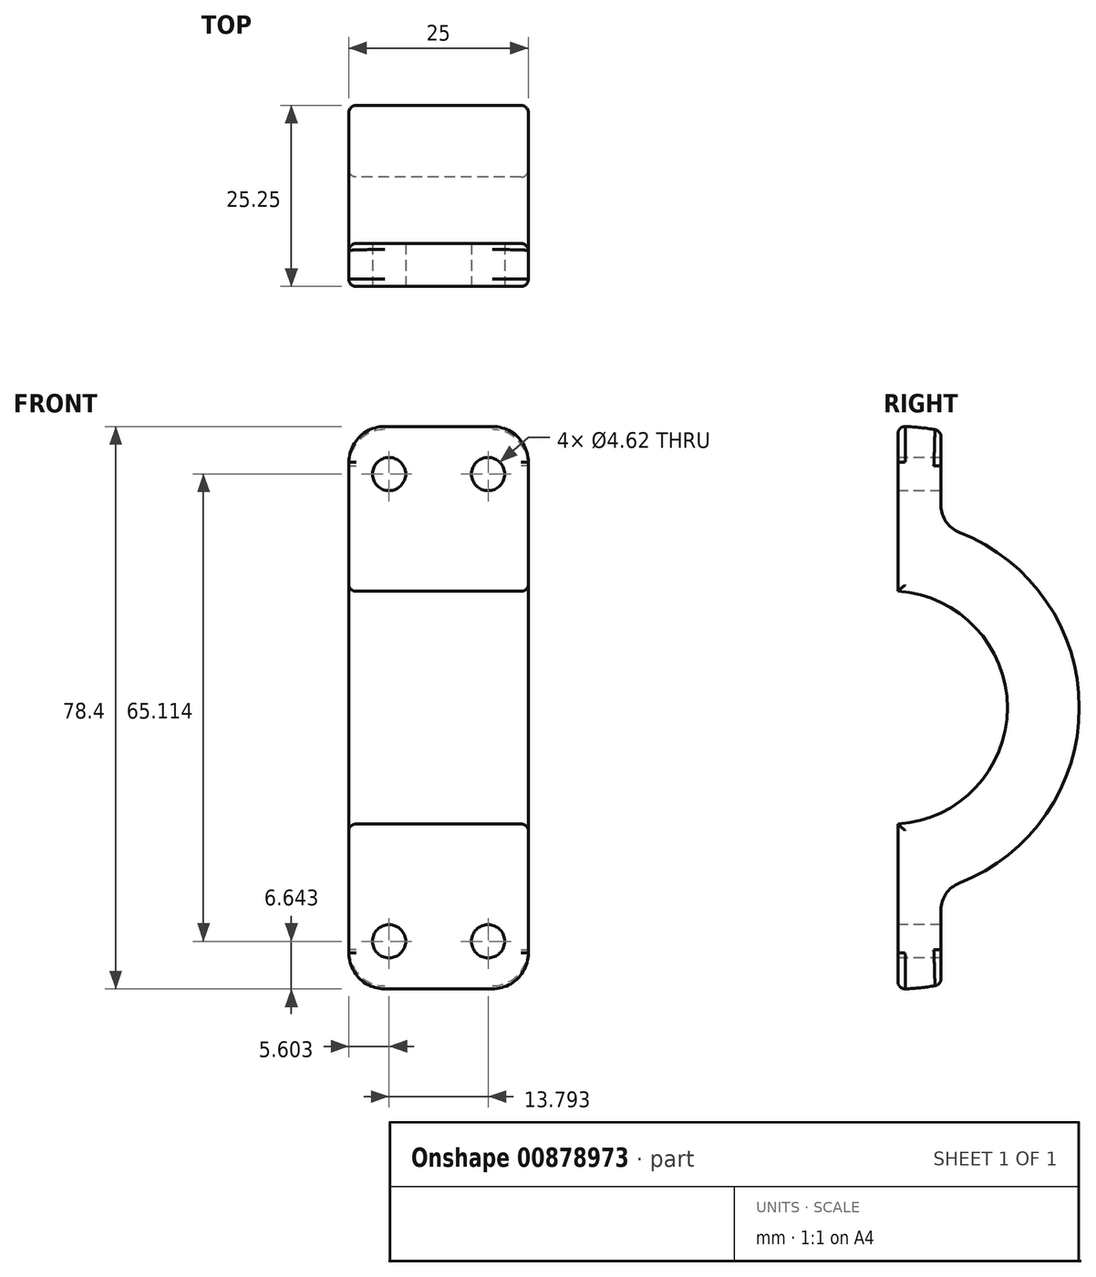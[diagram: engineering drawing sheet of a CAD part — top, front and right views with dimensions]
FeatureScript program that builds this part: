
annotation { "Feature Type Name" : "Feature", "Feature Type Description" : "" }
export const myFeature = defineFeature(function(context is Context, id is Id, definition is map)
    precondition{}
    {
        {
            var Q0;
            Q0=qCreatedBy(makeId("Right.planeOp"),FACE);
            var sketch = newSketch(context, id + "F0", { "sketchPlane" : qUnion([Q0])});
            skArc(sketch, "E0", {"start": v(1, -16.22) * mm, "mid": v(16.25, 0) * mm, "end": v(1, 16.22) * mm});
            skArc(sketch, "E1.0", {"start": v(9.54, -24.45) * mm, "mid": v(26.25, 0) * mm, "end": v(9.54, 24.45) * mm});
            skLineSegment(sketch, "E2.0", {"start": v(7, -28.18) * mm, "end": v(7, -38.62) * mm});
            skLineSegment(sketch, "E3.0", {"start": v(7, 28.18) * mm, "end": v(7, 38.62) * mm});
            skArc(sketch, "E4.0", {"start": v(1, -39.24) * mm, "mid": v(4.01, -39.04) * mm, "end": v(7, -38.62) * mm});
            skArc(sketch, "E5.trimOffspring", {"start": v(7, 38.62) * mm, "mid": v(4.01, 39.04) * mm, "end": v(1, 39.24) * mm});
            skPoint(sketch, "E6.visualSharp", {"position": v(-5, 25.77) * mm});
            skPoint(sketch, "E7.visualSharp", {"position": v(7, 25.3) * mm});
            skArc(sketch, "E7.filletArc", {"start": v(7, 28.18) * mm, "mid": v(7.7, 25.92) * mm, "end": v(9.54, 24.45) * mm});
            skPoint(sketch, "E8.visualSharp", {"position": v(7, -25.3) * mm});
            skArc(sketch, "E8.filletArc", {"start": v(9.54, -24.45) * mm, "mid": v(7.7, -25.92) * mm, "end": v(7, -28.18) * mm});
            skPoint(sketch, "E9.visualSharp", {"position": v(-5, -25.77) * mm});
            skLineSegment(sketch, "E10.0", {"start": v(1, 16.22) * mm, "end": v(1, 39.25) * mm});
            skLineSegment(sketch, "E11.0", {"start": v(1, -16.22) * mm, "end": v(1, -39.25) * mm});
            skSolve(sketch);
        }
        {
            var Q0;
            Q0=qSketchRegion(id+"F0",true);
            extrude(context, id + "F1", {"entities" : qUnion([Q0]), "endBound" : BoundingType.SYMMETRIC, "depth" : 25 * mm, "offsetDistance" : 25 * mm});
        }
        {
            var Q0;
            Q0=qCreatedBy(makeId("Front.planeOp"),FACE);
            var sketch = newSketch(context, id + "F2", { "sketchPlane" : qUnion([Q0])});
            skCircle(sketch, "E12", {"center": v(6.9, 32.56) * mm, "radius": 2.31 * mm});
            skCircle(sketch, "E13.MirrorC", {"center": v(-6.9, 32.56) * mm, "radius": 2.31 * mm});
            skCircle(sketch, "E14.MirrorC", {"center": v(-6.9, -32.56) * mm, "radius": 2.31 * mm});
            skCircle(sketch, "E15.MirrorC", {"center": v(6.9, -32.56) * mm, "radius": 2.31 * mm});
            skSolve(sketch);
        }
        {
            var Q0;
            Q0=qSketchRegion(id+"F2",true);
            extrude(context, id + "F3", {"entities" : qUnion([Q0]), "operationType" : NewBodyOperationType.REMOVE, "endBound" : BoundingType.THROUGH_ALL, "oppositeDirection" : true, "depth" : 25 * mm, "offsetDistance" : 25 * mm});
        }
        {
            var Q0;
            Q0=makeQuery(id+"F1.opExtrude","CAP_EDGE",EDGE,{"disambiguationData":[OSD([sQuery(id+"F0.wireOp",EDGE,"E5.trimOffspring")])],"isStart":false});
            var Q1;
            Q1=makeQuery(id+"F1.opExtrude","CAP_EDGE",EDGE,{"disambiguationData":[OSD([sQuery(id+"F0.wireOp",EDGE,"E5.trimOffspring")])],"isStart":true});
            var Q2;
            Q2=makeQuery(id+"F1.opExtrude","CAP_EDGE",EDGE,{"disambiguationData":[OSD([sQuery(id+"F0.wireOp",EDGE,"E4.0")])],"isStart":false});
            var Q3;
            Q3=makeQuery(id+"F1.opExtrude","CAP_EDGE",EDGE,{"disambiguationData":[OSD([sQuery(id+"F0.wireOp",EDGE,"E4.0")])],"isStart":true});
            fillet(context, id + "F4", {"entities" : qUnion([Q0, Q1, Q2, Q3]), "radius" : 5 * mm, "tangentPropagation" : true, "allowEdgeOverflow" : false});
        }
        {
            var Q0;
            Q0=makeQuery(id+"F1.opExtrude","CAP_FACE",FACE,{"disambiguationData":[OSD([sQuery(id+"F0.wireOp",EDGE,"E0"),sQuery(id+"F0.wireOp",EDGE,"E1.0"),sQuery(id+"F0.wireOp",EDGE,"g6IvzIde-RPpm-J4Ch-rFcU-dSb5MLyEbczB"),sQuery(id+"F0.wireOp",EDGE,"LpNSRWhE-LSOE-Vq07-Rzua-Ym4zSv88PilT"),sQuery(id+"F0.wireOp",EDGE,"E2.0"),sQuery(id+"F0.wireOp",EDGE,"E3.0"),sQuery(id+"F0.wireOp",EDGE,"E4.0"),sQuery(id+"F0.wireOp",EDGE,"E5.trimOffspring"),sQuery(id+"F0.wireOp",EDGE,"E7.filletArc"),sQuery(id+"F0.wireOp",EDGE,"E8.filletArc")])],"isStart":true});
            var Q1;
            Q1=makeQuery(id+"F1.opExtrude","CAP_FACE",FACE,{"disambiguationData":[OSD([sQuery(id+"F0.wireOp",EDGE,"E0"),sQuery(id+"F0.wireOp",EDGE,"E1.0"),sQuery(id+"F0.wireOp",EDGE,"g6IvzIde-RPpm-J4Ch-rFcU-dSb5MLyEbczB"),sQuery(id+"F0.wireOp",EDGE,"LpNSRWhE-LSOE-Vq07-Rzua-Ym4zSv88PilT"),sQuery(id+"F0.wireOp",EDGE,"E2.0"),sQuery(id+"F0.wireOp",EDGE,"E3.0"),sQuery(id+"F0.wireOp",EDGE,"E4.0"),sQuery(id+"F0.wireOp",EDGE,"E5.trimOffspring"),sQuery(id+"F0.wireOp",EDGE,"E7.filletArc"),sQuery(id+"F0.wireOp",EDGE,"E8.filletArc")])],"isStart":false});
            fillet(context, id + "F5", {"entities" : qUnion([Q0, Q1]), "radius" : 1 * mm, "tangentPropagation" : true, "allowEdgeOverflow" : false});
        }
    });
